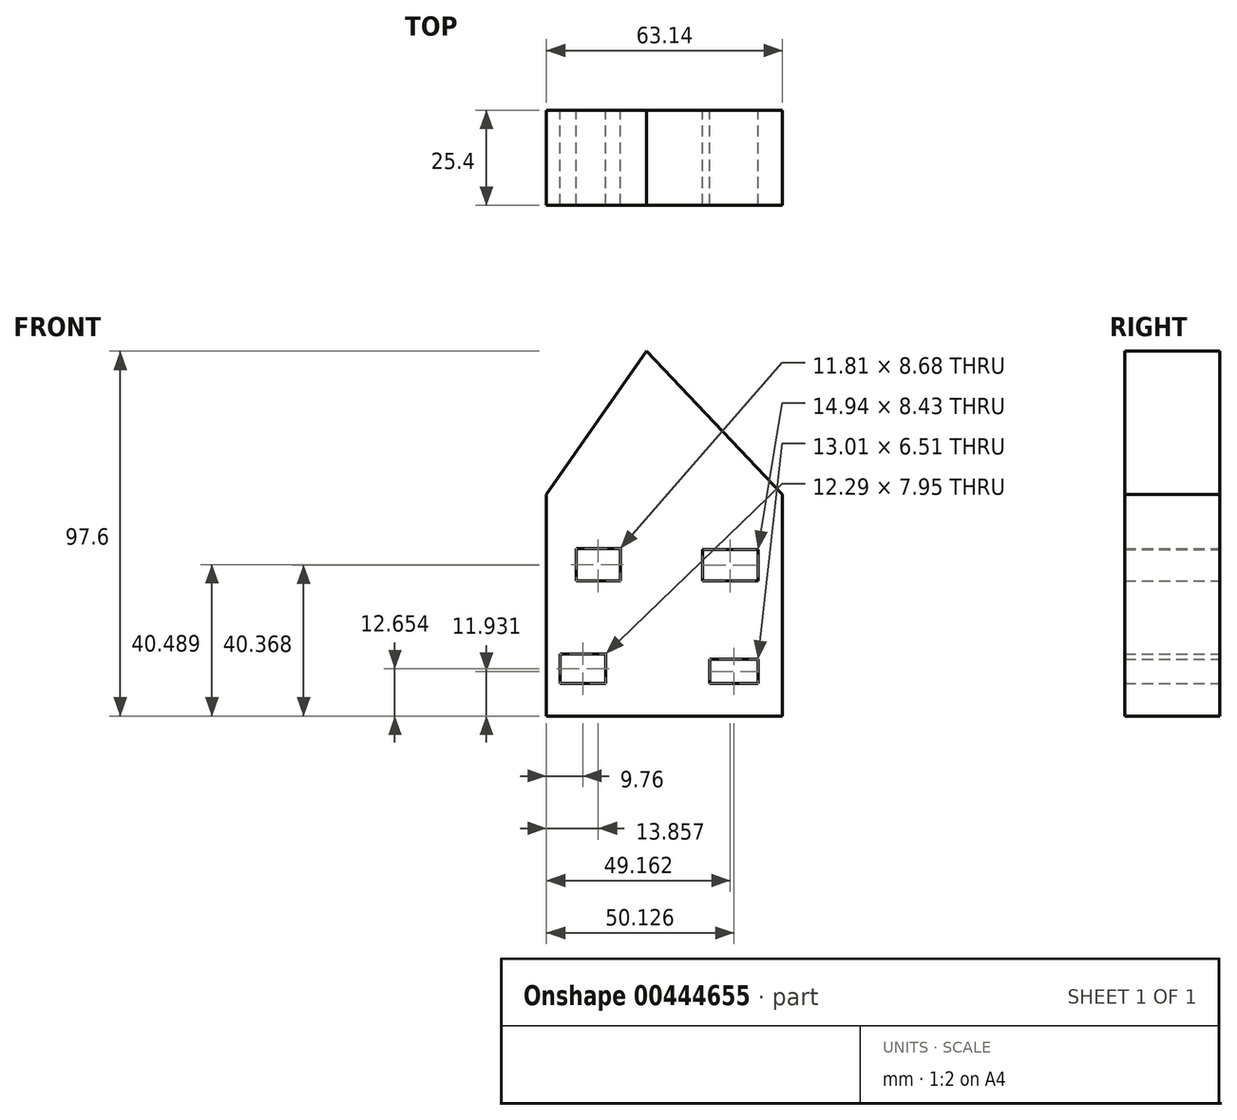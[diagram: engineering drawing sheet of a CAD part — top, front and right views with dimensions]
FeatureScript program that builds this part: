
annotation { "Feature Type Name" : "Feature", "Feature Type Description" : "" }
export const myFeature = defineFeature(function(context is Context, id is Id, definition is map)
    precondition{}
    {
        {
            var Q0;
            Q0=qCreatedBy(makeId("Front.planeOp"),FACE);
            var sketch = newSketch(context, id + "F0", { "sketchPlane" : qUnion([Q0])});
            skLineSegment(sketch, "E0.bottom", {"start": v(-26.75, 18.56) * mm, "end": v(36.4, 18.56) * mm});
            skLineSegment(sketch, "E0.left", {"start": v(-26.75, 18.56) * mm, "end": v(-26.75, -40.73) * mm});
            skLineSegment(sketch, "E0.right", {"start": v(36.4, 18.56) * mm, "end": v(36.4, -40.73) * mm});
            skLineSegment(sketch, "E1", {"start": v(-26.75, 18.56) * mm, "end": v(0, 56.87) * mm});
            skLineSegment(sketch, "E2", {"start": v(0, 56.87) * mm, "end": v(36.4, 18.56) * mm});
            skLineSegment(sketch, "E3.bottom", {"start": v(-18.8, 4.1) * mm, "end": v(-6.99, 4.1) * mm});
            skLineSegment(sketch, "E3.top", {"start": v(-18.8, -4.58) * mm, "end": v(-6.99, -4.58) * mm});
            skLineSegment(sketch, "E3.left", {"start": v(-18.8, 4.1) * mm, "end": v(-18.8, -4.58) * mm});
            skLineSegment(sketch, "E3.right", {"start": v(-6.99, 4.1) * mm, "end": v(-6.99, -4.58) * mm});
            skLineSegment(sketch, "E4.bottom", {"start": v(14.94, 3.86) * mm, "end": v(29.88, 3.86) * mm});
            skLineSegment(sketch, "E4.top", {"start": v(14.94, -4.58) * mm, "end": v(29.88, -4.58) * mm});
            skLineSegment(sketch, "E4.left", {"start": v(14.94, 3.86) * mm, "end": v(14.94, -4.58) * mm});
            skLineSegment(sketch, "E4.right", {"start": v(29.88, 3.86) * mm, "end": v(29.88, -4.58) * mm});
            skLineSegment(sketch, "E5.bottom", {"start": v(16.87, -25.55) * mm, "end": v(29.88, -25.55) * mm});
            skLineSegment(sketch, "E5.top", {"start": v(16.87, -32.05) * mm, "end": v(29.88, -32.05) * mm});
            skLineSegment(sketch, "E5.left", {"start": v(16.87, -25.55) * mm, "end": v(16.87, -32.05) * mm});
            skLineSegment(sketch, "E5.right", {"start": v(29.88, -25.55) * mm, "end": v(29.88, -32.05) * mm});
            skPoint(sketch, "E6.oppositeSnap0", {"position": v(23.38, -32.05) * mm});
            skLineSegment(sketch, "E6.bottom", {"start": v(-23.14, -24.1) * mm, "end": v(-10.84, -24.1) * mm});
            skLineSegment(sketch, "E6.top", {"start": v(-23.14, -32.05) * mm, "end": v(-10.84, -32.05) * mm});
            skLineSegment(sketch, "E6.left", {"start": v(-23.14, -24.1) * mm, "end": v(-23.14, -32.05) * mm});
            skLineSegment(sketch, "E6.right", {"start": v(-10.84, -24.1) * mm, "end": v(-10.84, -32.05) * mm});
            skLineSegment(sketch, "E7", {"start": v(-26.75, -40.73) * mm, "end": v(36.4, -40.73) * mm});
            skLineSegment(sketch, "E8.bottom", {"start": v(-2.9, -40.73) * mm, "end": v(7.71, -40.73) * mm});
            skLineSegment(sketch, "E8.top", {"start": v(-2.9, -27.23) * mm, "end": v(7.71, -27.23) * mm});
            skLineSegment(sketch, "E8.left", {"start": v(-2.9, -40.73) * mm, "end": v(-2.9, -27.23) * mm});
            skLineSegment(sketch, "E8.right", {"start": v(7.71, -40.73) * mm, "end": v(7.71, -27.23) * mm});
            skSolve(sketch);
        }
        {
            var Q0;
            Q0 = qSketchRegion(id + "F0", true);
            extrude(context, id + "F1", {"entities" : qUnion([Q0]), "depth" : 25.4 * mm});
        }
        {
            var Q0;
            Q0 = qSketchRegion(id + "F0", true);
            extrude(context, id + "F2", {"entities" : qUnion([Q0]), "operationType" : NewBodyOperationType.ADD, "depth" : 25.4 * mm});
        }
    });
